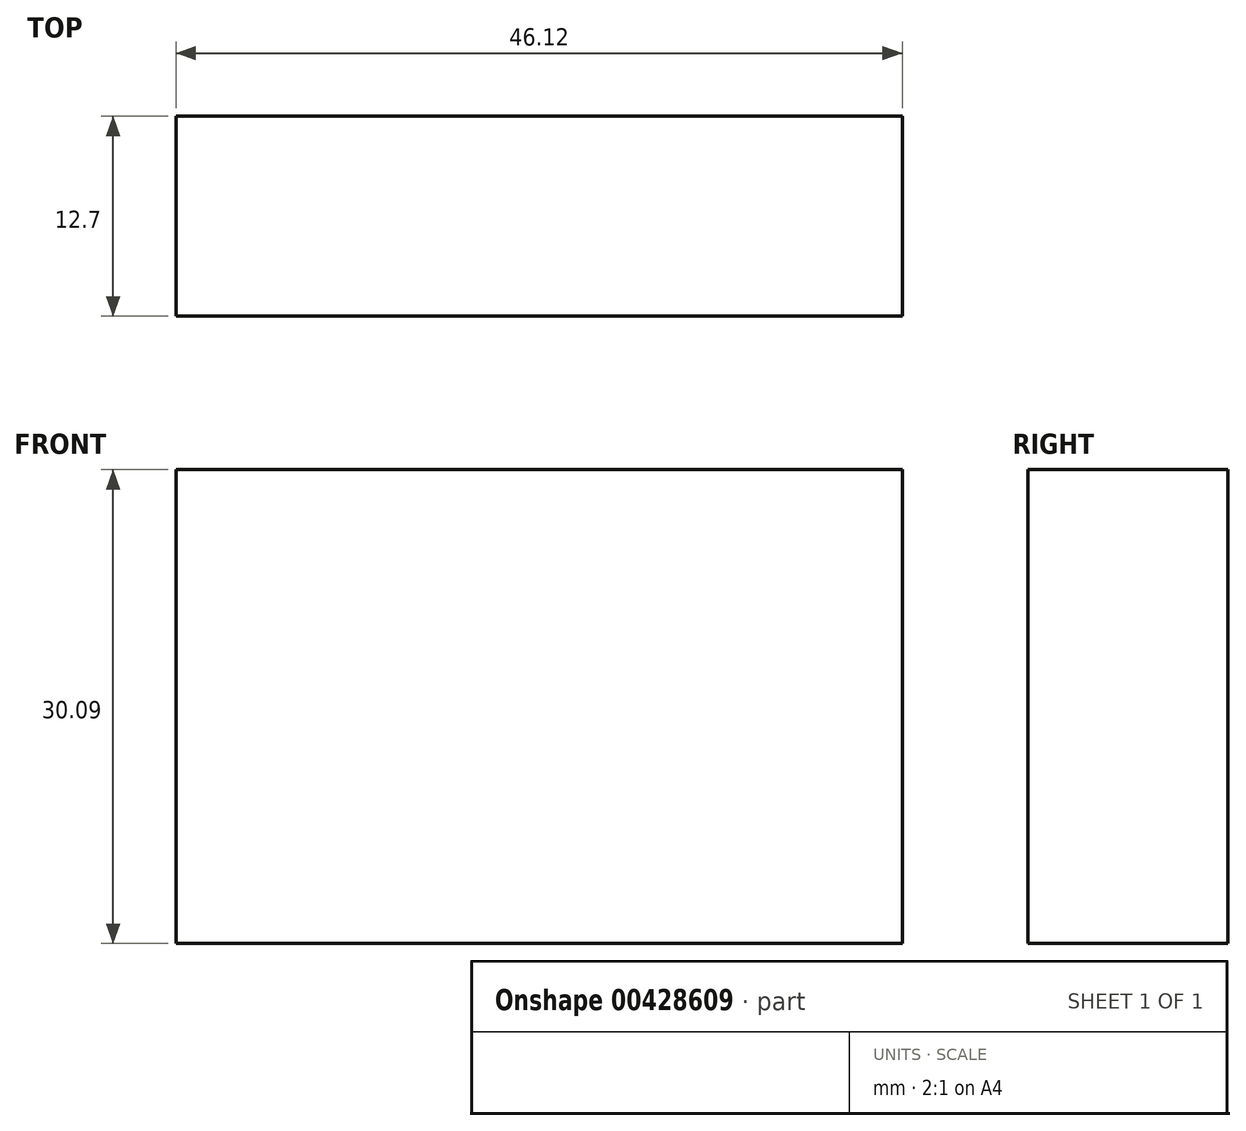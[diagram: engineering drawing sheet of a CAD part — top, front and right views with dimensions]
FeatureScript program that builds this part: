
annotation { "Feature Type Name" : "Feature", "Feature Type Description" : "" }
export const myFeature = defineFeature(function(context is Context, id is Id, definition is map)
    precondition{}
    {
        {
            var Q0;
            Q0=qCreatedBy(makeId("Front.planeOp"),FACE);
            var sketch = newSketch(context, id + "F0", { "sketchPlane" : qUnion([Q0])});
            skLineSegment(sketch, "E0.bottom", {"start": v(-63.42, 56.64) * mm, "end": v(-17.3, 56.64) * mm});
            skLineSegment(sketch, "E0.top", {"start": v(-63.42, 26.55) * mm, "end": v(-17.3, 26.55) * mm});
            skLineSegment(sketch, "E0.left", {"start": v(-63.42, 56.64) * mm, "end": v(-63.42, 26.55) * mm});
            skLineSegment(sketch, "E0.right", {"start": v(-17.3, 56.64) * mm, "end": v(-17.3, 26.55) * mm});
            skSolve(sketch);
        }
        {
            var Q0;
            Q0=makeQuery(id+"F0.imprint","IMPRINT",FACE,{"disambiguationData":[TD([[makeQuery(id+"F0.imprint","IMPRINT",EDGE,{"derivedFrom":sQuery(id+"F0.wireOp",EDGE,"E0.bottom")}),-1.0]])]});
            extrude(context, id + "F1", {"entities" : qUnion([Q0]), "depth" : 12.7 * mm});
        }
    });
